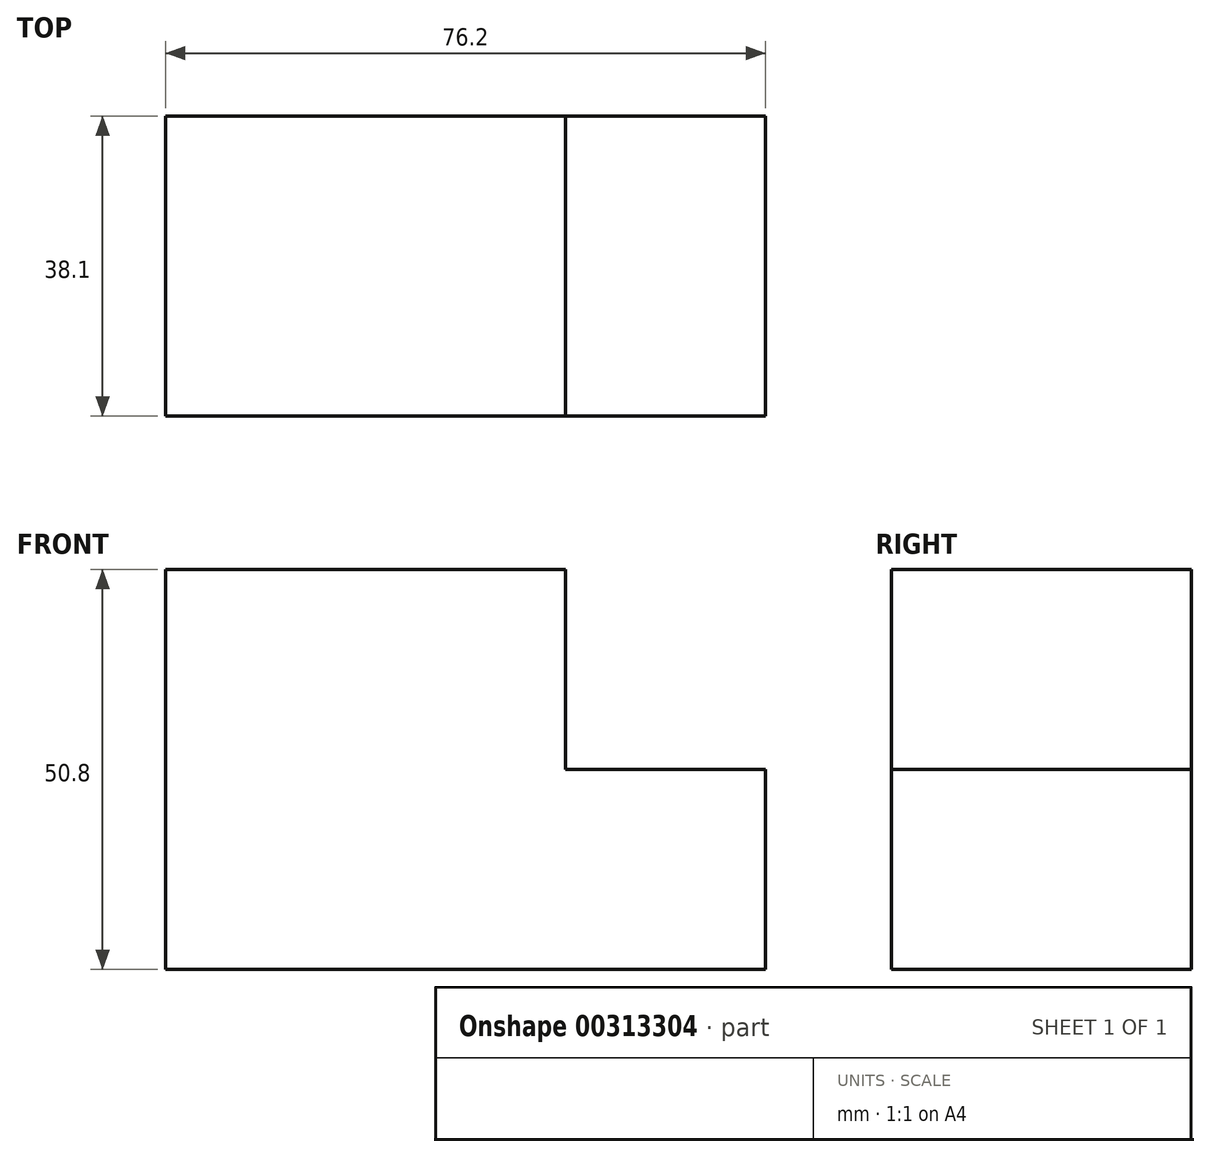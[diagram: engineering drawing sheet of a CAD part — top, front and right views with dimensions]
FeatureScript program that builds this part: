
annotation { "Feature Type Name" : "Feature", "Feature Type Description" : "" }
export const myFeature = defineFeature(function(context is Context, id is Id, definition is map)
    precondition{}
    {
        {
            var Q0;
            Q0=qCreatedBy(makeId("Front.planeOp"),FACE);
            var sketch = newSketch(context, id + "F0", { "sketchPlane" : qUnion([Q0])});
            skLineSegment(sketch, "E0", {"start": v(-30.97, -37.84) * mm, "end": v(45.23, -37.84) * mm});
            skLineSegment(sketch, "E1", {"start": v(45.23, -37.84) * mm, "end": v(45.23, -12.44) * mm});
            skLineSegment(sketch, "E2", {"start": v(45.23, -12.44) * mm, "end": v(19.83, -12.44) * mm});
            skLineSegment(sketch, "E3", {"start": v(19.83, -12.44) * mm, "end": v(19.83, 12.96) * mm});
            skLineSegment(sketch, "E4", {"start": v(19.83, 12.96) * mm, "end": v(-30.97, 12.96) * mm});
            skLineSegment(sketch, "E5", {"start": v(-30.97, 12.96) * mm, "end": v(-30.97, -37.84) * mm});
            skSolve(sketch);
        }
        {
            var Q0;
            Q0 = qSketchRegion(id + "F0", true);
            extrude(context, id + "F1", {"entities" : qUnion([Q0]), "depth" : 38.1 * mm});
        }
    });
